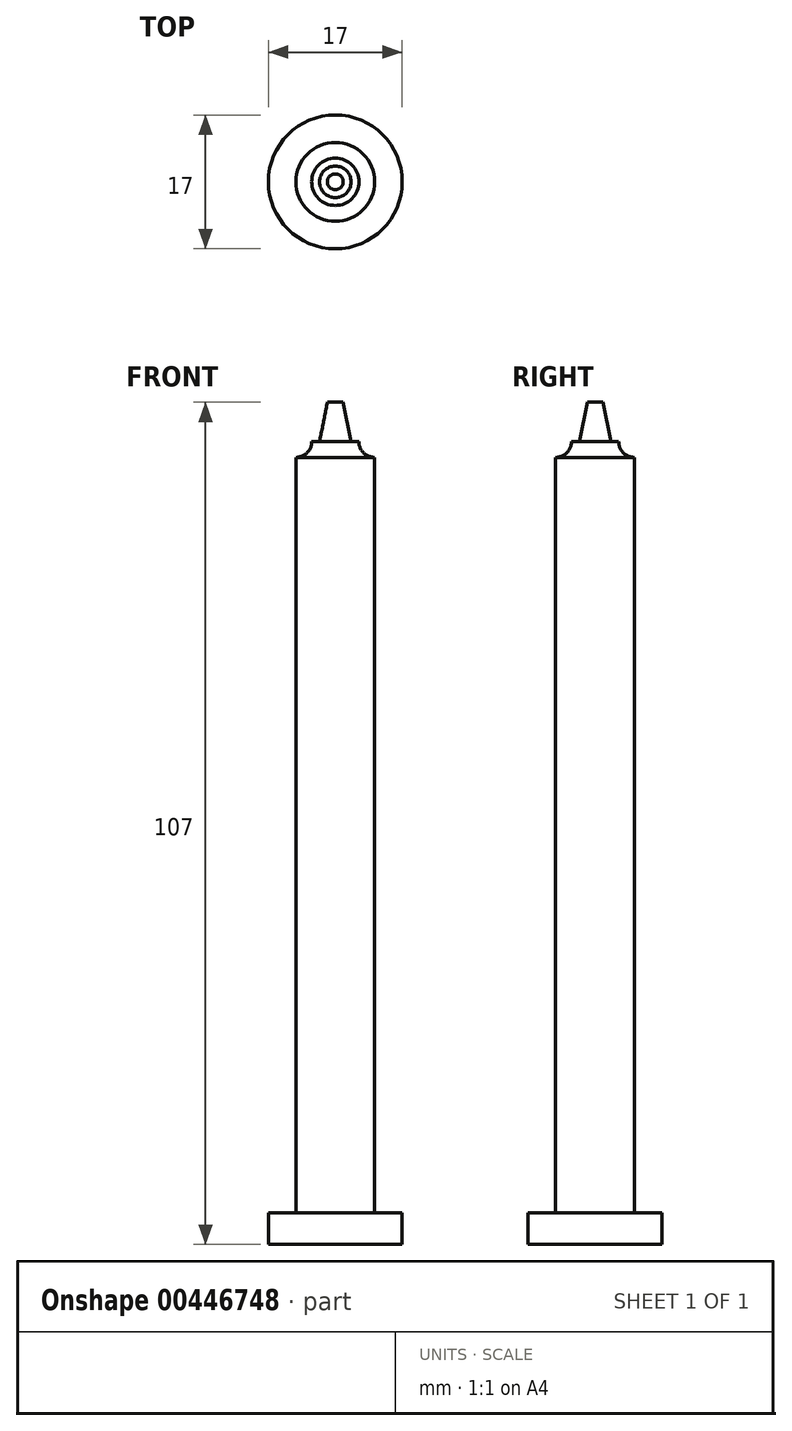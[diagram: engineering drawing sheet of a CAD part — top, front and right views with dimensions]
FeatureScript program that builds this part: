
annotation { "Feature Type Name" : "Feature", "Feature Type Description" : "" }
export const myFeature = defineFeature(function(context is Context, id is Id, definition is map)
    precondition{}
    {
        {
            var Q0;
            Q0=qCreatedBy(makeId("Top.planeOp"),FACE);
            var sketch = newSketch(context, id + "F0", { "sketchPlane" : qUnion([Q0])});
            skCircle(sketch, "E0", {"center": v(0, 0) * mm, "radius": 8.5 * mm});
            skSolve(sketch);
        }
        {
            var Q0;
            Q0=qSketchRegion(id+"F0",true);
            extrude(context, id + "F1", {"entities" : qUnion([Q0]), "depth" : 4 * mm});
        }
        {
            var Q0;
            Q0=qCreatedBy(makeId("Top.planeOp"),FACE);
            var sketch = newSketch(context, id + "F2", { "sketchPlane" : qUnion([Q0])});
            skCircle(sketch, "E1", {"center": v(0, 0) * mm, "radius": 5 * mm});
            skSolve(sketch);
        }
        {
            var Q0;
            Q0=qSketchRegion(id+"F2",true);
            extrude(context, id + "F3", {"entities" : qUnion([Q0]), "operationType" : NewBodyOperationType.ADD, "depth" : 100 * mm});
        }
        {
            var Q0;
            Q0=qCreatedBy(makeId("Right.planeOp"),FACE);
            var sketch = newSketch(context, id + "F4", { "sketchPlane" : qUnion([Q0])});
            skLineSegment(sketch, "E2", {"start": v(0, 102) * mm, "end": v(0, 100) * mm});
            skLineSegment(sketch, "E3", {"start": v(0, 100) * mm, "end": v(5, 100) * mm});
            skLineSegment(sketch, "E4", {"start": v(3, 102) * mm, "end": v(0, 102) * mm});
            skArc(sketch, "E5", {"start": v(3, 102) * mm, "mid": v(3.59, 100.59) * mm, "end": v(5, 100) * mm});
            skSolve(sketch);
        }
        {
            var Q0;
            Q0=makeQuery(id+"F4.imprint","IMPRINT",FACE,{"disambiguationData":[TD([[makeQuery(id+"F4.imprint","IMPRINT",EDGE,{"derivedFrom":sQuery(id+"F4.wireOp",EDGE,"E2")}),1.0]])]});
            var Q1;
            Q1=sQuery(id+"F4.wireOp",EDGE,"E2");
            revolve(context, id + "F5", {"operationType" : NewBodyOperationType.ADD, "entities" : qUnion([Q0]), "axis" : qUnion([Q1]), "revolveType" : RevolveType.FULL});
        }
        {
            var Q0;
            Q0=qCreatedBy(makeId("Right.planeOp"),FACE);
            var sketch = newSketch(context, id + "F6", { "sketchPlane" : qUnion([Q0])});
            skLineSegment(sketch, "E6", {"start": v(0, 102) * mm, "end": v(0, 107) * mm});
            skLineSegment(sketch, "E7", {"start": v(0, 107) * mm, "end": v(1, 107) * mm});
            skLineSegment(sketch, "E8", {"start": v(1, 107) * mm, "end": v(2, 102) * mm});
            skLineSegment(sketch, "E9", {"start": v(2, 102) * mm, "end": v(0, 102) * mm});
            skSolve(sketch);
        }
        {
            var Q0;
            Q0=makeQuery(id+"F6.imprint","IMPRINT",FACE,{"disambiguationData":[TD([[makeQuery(id+"F6.imprint","IMPRINT",EDGE,{"derivedFrom":sQuery(id+"F6.wireOp",EDGE,"E6")}),-1.0]])]});
            var Q1;
            Q1=sQuery(id+"F6.wireOp",EDGE,"E6");
            revolve(context, id + "F7", {"operationType" : NewBodyOperationType.ADD, "entities" : qUnion([Q0]), "axis" : qUnion([Q1]), "revolveType" : RevolveType.FULL});
        }
    });
